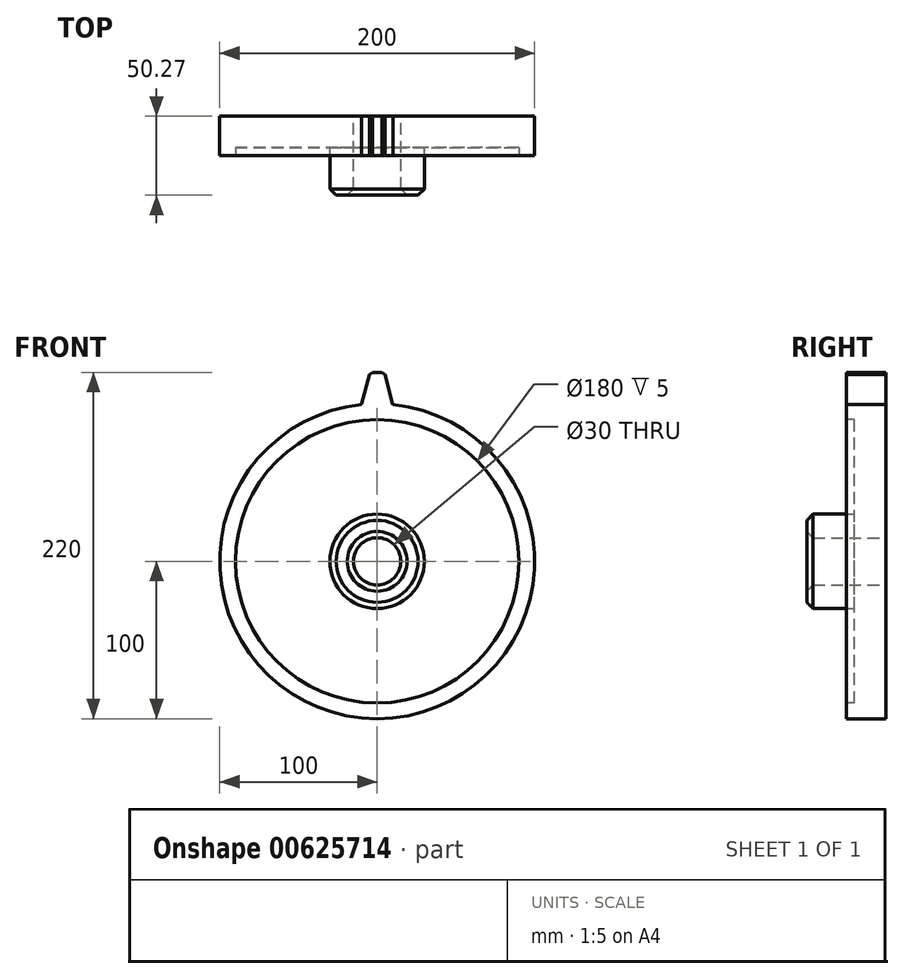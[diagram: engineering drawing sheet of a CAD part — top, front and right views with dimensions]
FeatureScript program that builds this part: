
annotation { "Feature Type Name" : "Feature", "Feature Type Description" : "" }
export const myFeature = defineFeature(function(context is Context, id is Id, definition is map)
    precondition{}
    {
        {
            var Q0;
            Q0=qCreatedBy(makeId("Front.planeOp"),FACE);
            var sketch = newSketch(context, id + "F0", { "sketchPlane" : qUnion([Q0])});
            skCircle(sketch, "E0", {"center": v(0, 0) * mm, "radius": 100 * mm});
            skLineSegment(sketch, "E1", {"start": v(-6.5, 99.79) * mm, "end": v(2, 125.59) * mm});
            skLineSegment(sketch, "E2", {"start": v(2, 125.59) * mm, "end": v(8.54, 125.59) * mm});
            skLineSegment(sketch, "E3", {"start": v(8.54, 125.59) * mm, "end": v(14.1, 99) * mm});
            skSolve(sketch);
        }
        {
            var Q0;
            {var subQ0=sQuery(id+"F0.wireOp",EDGE,"E0");var subQ1=makeQuery(id+"F0.imprint","INTERSECT",VERTEX,{"derivedFrom":[subQ0,sQuery(id+"F0.wireOp",EDGE,"E1")]});Q0=makeQuery(id+"F0.imprint","IMPRINT",FACE,{"disambiguationData":[TD([[makeQuery(id+"F0.imprint","IMPRINT",EDGE,{"disambiguationData":[TD([[subQ1,1.0]])],"derivedFrom":subQ0}),1.0]])]});}
            extrude(context, id + "F1", {"entities" : qUnion([Q0]), "depth" : 25 * mm, "offsetDistance" : 25 * mm});
        }
        {
            var Q0;
            Q0=makeQuery(id+"F1.opExtrude","CAP_FACE",FACE,{"disambiguationData":[OSD([sQuery(id+"F0.wireOp",EDGE,"E0")])],"isStart":false});
            var sketch = newSketch(context, id + "F2", { "sketchPlane" : qUnion([Q0])});
            skLineSegment(sketch, "E4", {"start": v(10, 99.5) * mm, "end": v(4.5, 120) * mm});
            skLineSegment(sketch, "E5", {"start": v(4.5, 120) * mm, "end": v(-4.5, 120) * mm});
            skLineSegment(sketch, "E6", {"start": v(-4.5, 120) * mm, "end": v(-10, 99.5) * mm});
            skLineSegment(sketch, "E7", {"start": v(-10, 99.5) * mm, "end": v(10, 99.5) * mm});
            skSolve(sketch);
        }
        {
            var Q0;
            {var subQ0=sQuery(id+"F2.wireOp",EDGE,"E4");Q0=makeQuery(id+"F2.imprint","IMPRINT",FACE,{"disambiguationData":[TD([[makeQuery(id+"F2.imprint","IMPRINT",EDGE,{"derivedFrom":subQ0}),1.0]])]});}
            extrude(context, id + "F3", {"entities" : qUnion([Q0]), "operationType" : NewBodyOperationType.ADD, "oppositeDirection" : true, "depth" : 25 * mm, "offsetDistance" : 25 * mm});
        }
        {
            var Q0;
            Q0=makeQuery(id+"F3.opExtrude","SWEPT_EDGE",EDGE,{"disambiguationData":[OSD([sQuery(id+"F2.wireOp",EDGE,"E5"),sQuery(id+"F2.wireOp",EDGE,"E6")])]});
            var Q1;
            Q1=makeQuery(id+"F3.opExtrude","SWEPT_EDGE",EDGE,{"disambiguationData":[OSD([sQuery(id+"F2.wireOp",EDGE,"E4"),sQuery(id+"F2.wireOp",EDGE,"E5")])]});
            chamfer(context, id + "F4", {"entities" : qUnion([Q0, Q1]), "width" : 2 * mm, "tangentPropagation" : true});
        }
        {
            var Q0;
            Q0=makeQuery(id+"F3.opExtrude","SWEPT_EDGE",EDGE,{"disambiguationData":[OSD([sQuery(id+"F0.wireOp",EDGE,"E0"),sQuery(id+"F2.wireOp",EDGE,"E4"),sQuery(id+"F2.wireOp",EDGE,"E7")])]});
            var Q1;
            Q1=makeQuery(id+"F3.opExtrude","SWEPT_EDGE",EDGE,{"disambiguationData":[OSD([sQuery(id+"F0.wireOp",EDGE,"E0"),sQuery(id+"F2.wireOp",EDGE,"E6"),sQuery(id+"F2.wireOp",EDGE,"E7")])]});
            fillet(context, id + "F5", {"entities" : qUnion([Q0, Q1]), "radius" : 5 * mm, "tangentPropagation" : true, "allowEdgeOverflow" : false});
        }
        {
            var Q0;
            {var subQ0=sQuery(id+"F2.wireOp",EDGE,"E6");var subQ1=sQuery(id+"F2.wireOp",EDGE,"E5");var subQ2=sQuery(id+"F2.wireOp",EDGE,"E4");var subQ3=sQuery(id+"F0.wireOp",EDGE,"E0");Q0=makeQuery(id+"FQ06Kex2k1FlT4b_1.19.F3.boolean.opBoolean","MERGE",FACE,{"derivedFrom":[makeQuery(id+"FQ06Kex2k1FlT4b_1.18.F3.boolean.opBoolean","MERGE",FACE,{"derivedFrom":[makeQuery(id+"FQ06Kex2k1FlT4b_1.17.F3.boolean.opBoolean","MERGE",FACE,{"derivedFrom":[makeQuery(id+"FQ06Kex2k1FlT4b_1.16.F3.boolean.opBoolean","MERGE",FACE,{"derivedFrom":[makeQuery(id+"FQ06Kex2k1FlT4b_1.15.F3.boolean.opBoolean","MERGE",FACE,{"derivedFrom":[makeQuery(id+"FQ06Kex2k1FlT4b_1.14.F3.boolean.opBoolean","MERGE",FACE,{"derivedFrom":[makeQuery(id+"FQ06Kex2k1FlT4b_1.13.F3.boolean.opBoolean","MERGE",FACE,{"derivedFrom":[makeQuery(id+"FQ06Kex2k1FlT4b_1.12.F3.boolean.opBoolean","MERGE",FACE,{"derivedFrom":[makeQuery(id+"FQ06Kex2k1FlT4b_1.11.F3.boolean.opBoolean","MERGE",FACE,{"derivedFrom":[makeQuery(id+"FQ06Kex2k1FlT4b_1.10.F3.boolean.opBoolean","MERGE",FACE,{"derivedFrom":[makeQuery(id+"FQ06Kex2k1FlT4b_1.9.F3.boolean.opBoolean","MERGE",FACE,{"derivedFrom":[makeQuery(id+"FQ06Kex2k1FlT4b_1.8.F3.boolean.opBoolean","MERGE",FACE,{"derivedFrom":[makeQuery(id+"FQ06Kex2k1FlT4b_1.7.F3.boolean.opBoolean","MERGE",FACE,{"derivedFrom":[makeQuery(id+"FQ06Kex2k1FlT4b_1.6.F3.boolean.opBoolean","MERGE",FACE,{"derivedFrom":[makeQuery(id+"FQ06Kex2k1FlT4b_1.5.F3.boolean.opBoolean","MERGE",FACE,{"derivedFrom":[makeQuery(id+"FQ06Kex2k1FlT4b_1.4.F3.boolean.opBoolean","MERGE",FACE,{"derivedFrom":[makeQuery(id+"FQ06Kex2k1FlT4b_1.3.F3.boolean.opBoolean","MERGE",FACE,{"derivedFrom":[makeQuery(id+"FQ06Kex2k1FlT4b_1.2.F3.boolean.opBoolean","MERGE",FACE,{"derivedFrom":[makeQuery(id+"FQ06Kex2k1FlT4b_1.1.F3.boolean.opBoolean","MERGE",FACE,{"derivedFrom":[makeQuery(id+"F3.boolean.opBoolean","MERGE",FACE,{"derivedFrom":[makeQuery(id+"F1.opExtrude","CAP_FACE",FACE,{"disambiguationData":[OSD([subQ3])],"isStart":false}),makeQuery(id+"F3.opExtrude","CAP_FACE",FACE,{"disambiguationData":[OSD([subQ3,subQ2,subQ1,subQ0])],"isStart":true})]}),makeQuery(id+"FQ06Kex2k1FlT4b_1.1.F3.opExtrude","CAP_FACE",FACE,{"disambiguationData":[OSD([subQ3,subQ2,subQ1,subQ0])],"isStart":true})]}),makeQuery(id+"FQ06Kex2k1FlT4b_1.2.F3.opExtrude","CAP_FACE",FACE,{"disambiguationData":[OSD([subQ3,subQ2,subQ1,subQ0])],"isStart":true})]}),makeQuery(id+"FQ06Kex2k1FlT4b_1.3.F3.opExtrude","CAP_FACE",FACE,{"disambiguationData":[OSD([subQ3,subQ2,subQ1,subQ0])],"isStart":true})]}),makeQuery(id+"FQ06Kex2k1FlT4b_1.4.F3.opExtrude","CAP_FACE",FACE,{"disambiguationData":[OSD([subQ3,subQ2,subQ1,subQ0])],"isStart":true})]}),makeQuery(id+"FQ06Kex2k1FlT4b_1.5.F3.opExtrude","CAP_FACE",FACE,{"disambiguationData":[OSD([subQ3,subQ2,subQ1,subQ0])],"isStart":true})]}),makeQuery(id+"FQ06Kex2k1FlT4b_1.6.F3.opExtrude","CAP_FACE",FACE,{"disambiguationData":[OSD([subQ3,subQ2,subQ1,subQ0])],"isStart":true})]}),makeQuery(id+"FQ06Kex2k1FlT4b_1.7.F3.opExtrude","CAP_FACE",FACE,{"disambiguationData":[OSD([subQ3,subQ2,subQ1,subQ0])],"isStart":true})]}),makeQuery(id+"FQ06Kex2k1FlT4b_1.8.F3.opExtrude","CAP_FACE",FACE,{"disambiguationData":[OSD([subQ3,subQ2,subQ1,subQ0])],"isStart":true})]}),makeQuery(id+"FQ06Kex2k1FlT4b_1.9.F3.opExtrude","CAP_FACE",FACE,{"disambiguationData":[OSD([subQ3,subQ2,subQ1,subQ0])],"isStart":true})]}),makeQuery(id+"FQ06Kex2k1FlT4b_1.10.F3.opExtrude","CAP_FACE",FACE,{"disambiguationData":[OSD([subQ3,subQ2,subQ1,subQ0])],"isStart":true})]}),makeQuery(id+"FQ06Kex2k1FlT4b_1.11.F3.opExtrude","CAP_FACE",FACE,{"disambiguationData":[OSD([subQ3,subQ2,subQ1,subQ0])],"isStart":true})]}),makeQuery(id+"FQ06Kex2k1FlT4b_1.12.F3.opExtrude","CAP_FACE",FACE,{"disambiguationData":[OSD([subQ3,subQ2,subQ1,subQ0])],"isStart":true})]}),makeQuery(id+"FQ06Kex2k1FlT4b_1.13.F3.opExtrude","CAP_FACE",FACE,{"disambiguationData":[OSD([subQ3,subQ2,subQ1,subQ0])],"isStart":true})]}),makeQuery(id+"FQ06Kex2k1FlT4b_1.14.F3.opExtrude","CAP_FACE",FACE,{"disambiguationData":[OSD([subQ3,subQ2,subQ1,subQ0])],"isStart":true})]}),makeQuery(id+"FQ06Kex2k1FlT4b_1.15.F3.opExtrude","CAP_FACE",FACE,{"disambiguationData":[OSD([subQ3,subQ2,subQ1,subQ0])],"isStart":true})]}),makeQuery(id+"FQ06Kex2k1FlT4b_1.16.F3.opExtrude","CAP_FACE",FACE,{"disambiguationData":[OSD([subQ3,subQ2,subQ1,subQ0])],"isStart":true})]}),makeQuery(id+"FQ06Kex2k1FlT4b_1.17.F3.opExtrude","CAP_FACE",FACE,{"disambiguationData":[OSD([subQ3,subQ2,subQ1,subQ0])],"isStart":true})]}),makeQuery(id+"FQ06Kex2k1FlT4b_1.18.F3.opExtrude","CAP_FACE",FACE,{"disambiguationData":[OSD([subQ3,subQ2,subQ1,subQ0])],"isStart":true})]}),makeQuery(id+"FQ06Kex2k1FlT4b_1.19.F3.opExtrude","CAP_FACE",FACE,{"disambiguationData":[OSD([subQ3,subQ2,subQ1,subQ0])],"isStart":true})]});}
            var sketch = newSketch(context, id + "F6", { "sketchPlane" : qUnion([Q0])});
            skCircle(sketch, "E8", {"center": v(0, 0) * mm, "radius": 90 * mm});
            skSolve(sketch);
        }
        {
            var Q0;
            Q0=makeQuery(id+"F6.imprint","IMPRINT",FACE,{"disambiguationData":[TD([[makeQuery(id+"F6.imprint","IMPRINT",EDGE,{"derivedFrom":sQuery(id+"F6.wireOp",EDGE,"E8")}),1.0]])]});
            extrude(context, id + "F7", {"entities" : qUnion([Q0]), "operationType" : NewBodyOperationType.REMOVE, "oppositeDirection" : true, "depth" : 5 * mm, "offsetDistance" : 25 * mm});
        }
        {
            var Q0;
            Q0=makeQuery(id+"F7.boolean.opBoolean","COPY",FACE,{"derivedFrom":makeQuery(id+"F7.opExtrude","CAP_FACE",FACE,{"disambiguationData":[OSD([sQuery(id+"F6.wireOp",EDGE,"E8")])],"isStart":false})});
            var sketch = newSketch(context, id + "F8", { "sketchPlane" : qUnion([Q0])});
            skCircle(sketch, "E9", {"center": v(0, 0) * mm, "radius": 30 * mm});
            skCircle(sketch, "E10", {"center": v(0, 0) * mm, "radius": 15 * mm});
            skSolve(sketch);
        }
        {
            var Q0;
            Q0=makeQuery(id+"F8.imprint","IMPRINT",FACE,{"disambiguationData":[TD([[makeQuery(id+"F8.imprint","IMPRINT",EDGE,{"derivedFrom":sQuery(id+"F8.wireOp",EDGE,"E9")}),1.0]])]});
            extrude(context, id + "F9", {"entities" : qUnion([Q0]), "operationType" : NewBodyOperationType.ADD, "depth" : 30.27 * mm, "offsetDistance" : 25 * mm});
        }
        {
            var Q0;
            Q0=makeQuery(id+"F9.boolean.opBoolean","SPLIT",FACE,{"disambiguationData":[TD([makeQuery(id+"F9.opExtrude","SWEPT_FACE",FACE,{"disambiguationData":[OSD([sQuery(id+"F8.wireOp",EDGE,"E10")])]})])],"derivedFrom":makeQuery(id+"F7.boolean.opBoolean","COPY",FACE,{"derivedFrom":makeQuery(id+"F7.opExtrude","CAP_FACE",FACE,{"disambiguationData":[OSD([sQuery(id+"F6.wireOp",EDGE,"E8")])],"isStart":false})})});
            extrude(context, id + "F10", {"entities" : qUnion([Q0]), "operationType" : NewBodyOperationType.REMOVE, "endBound" : BoundingType.THROUGH_ALL, "oppositeDirection" : true, "depth" : 25 * mm, "offsetDistance" : 25 * mm});
        }
        {
            var Q0;
            Q0=makeQuery(id+"F9.opExtrude","CAP_EDGE",EDGE,{"disambiguationData":[OSD([sQuery(id+"F8.wireOp",EDGE,"E9")])],"isStart":false});
            var Q1;
            Q1=makeQuery(id+"F9.opExtrude","CAP_EDGE",EDGE,{"disambiguationData":[OSD([sQuery(id+"F8.wireOp",EDGE,"E10")])],"isStart":false});
            chamfer(context, id + "F11", {"entities" : qUnion([Q0, Q1]), "width" : 4 * mm, "tangentPropagation" : true});
        }
    });
